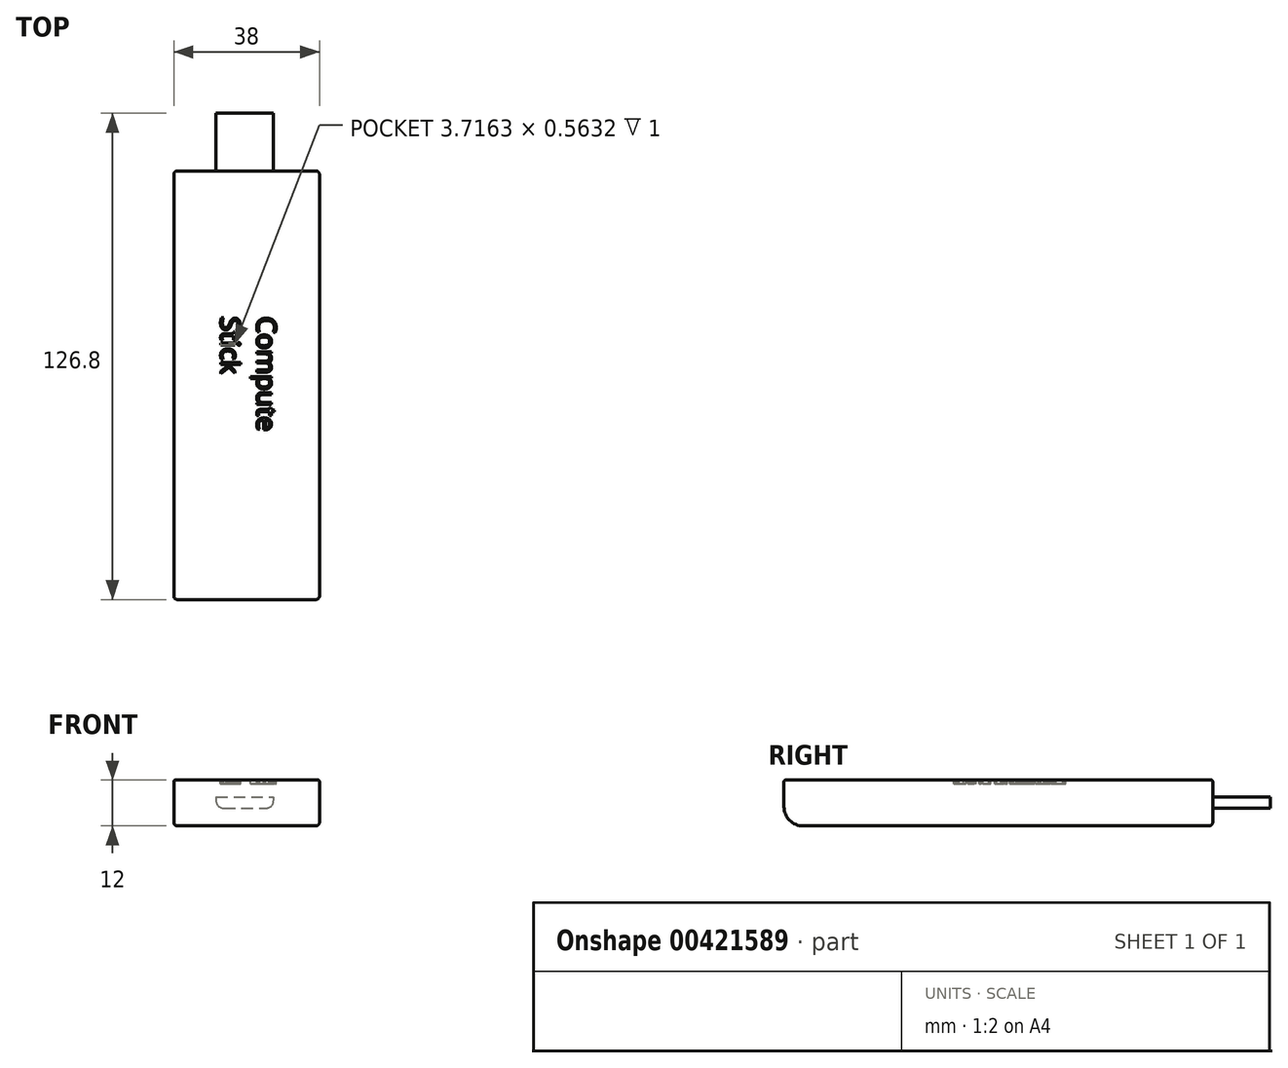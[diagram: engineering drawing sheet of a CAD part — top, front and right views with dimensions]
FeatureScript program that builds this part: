
annotation { "Feature Type Name" : "Feature", "Feature Type Description" : "" }
export const myFeature = defineFeature(function(context is Context, id is Id, definition is map)
    precondition{}
    {
        {
            var Q0;
            Q0=qCreatedBy(makeId("Top.planeOp"),FACE);
            var sketch = newSketch(context, id + "F0", { "sketchPlane" : qUnion([Q0])});
            skLineSegment(sketch, "E0.bottom", {"start": v(-18.53, 32.49) * mm, "end": v(19.47, 32.49) * mm});
            skLineSegment(sketch, "E0.top", {"start": v(-18.53, -79.31) * mm, "end": v(19.47, -79.31) * mm});
            skLineSegment(sketch, "E0.left", {"start": v(-18.53, 32.49) * mm, "end": v(-18.53, -79.31) * mm});
            skLineSegment(sketch, "E0.right", {"start": v(19.47, 32.49) * mm, "end": v(19.47, -79.31) * mm});
            skSolve(sketch);
        }
        {
            var Q0;
            Q0 = qSketchRegion(id + "F0", true);
            extrude(context, id + "F1", {"entities" : qUnion([Q0]), "depth" : 12 * mm, "offsetDistance" : 25 * mm});
        }
        {
            var Q0;
            Q0=makeQuery(id+"F1.opExtrude","SWEPT_EDGE",EDGE,{"disambiguationData":[OSD([sQuery(id+"F0.wireOp",EDGE,"E0.top"),sQuery(id+"F0.wireOp",EDGE,"E0.right")])]});
            var Q1;
            Q1=makeQuery(id+"F1.opExtrude","SWEPT_EDGE",EDGE,{"disambiguationData":[OSD([sQuery(id+"F0.wireOp",EDGE,"E0.top"),sQuery(id+"F0.wireOp",EDGE,"E0.left")])]});
            var Q2;
            Q2=makeQuery(id+"F1.opExtrude","SWEPT_EDGE",EDGE,{"disambiguationData":[OSD([sQuery(id+"F0.wireOp",EDGE,"E0.bottom"),sQuery(id+"F0.wireOp",EDGE,"E0.left")])]});
            var Q3;
            Q3=makeQuery(id+"F1.opExtrude","SWEPT_EDGE",EDGE,{"disambiguationData":[OSD([sQuery(id+"F0.wireOp",EDGE,"E0.bottom"),sQuery(id+"F0.wireOp",EDGE,"E0.right")])]});
            fillet(context, id + "F2", {"entities" : qUnion([Q0, Q1, Q2, Q3]), "radius" : 1 * mm, "tangentPropagation" : true, "allowEdgeOverflow" : false});
        }
        {
            var Q0;
            Q0=makeQuery(id+"F1.opExtrude","CAP_EDGE",EDGE,{"disambiguationData":[OSD([sQuery(id+"F0.wireOp",EDGE,"E0.top")])],"isStart":true});
            fillet(context, id + "F3", {"entities" : qUnion([Q0]), "radius" : 5 * mm, "allowEdgeOverflow" : false});
        }
        {
            var Q0;
            Q0=makeQuery(id+"F3.opFillet","BLEND_EDGE",EDGE,{"blendedFrom":[makeQuery(id+"F1.opExtrude","CAP_EDGE",EDGE,{"disambiguationData":[OSD([sQuery(id+"F0.wireOp",EDGE,"E0.top")])],"isStart":true}),makeQuery(id+"F1.opExtrude","SWEPT_FACE",FACE,{"disambiguationData":[OSD([sQuery(id+"F0.wireOp",EDGE,"E0.left")])]})],"blendedInto":[makeQuery(id+"F1.opExtrude","SWEPT_FACE",FACE,{"disambiguationData":[OSD([sQuery(id+"F0.wireOp",EDGE,"E0.left")])]})]});
            var Q1;
            Q1=makeQuery(id+"F1.opExtrude","CAP_EDGE",EDGE,{"disambiguationData":[OSD([sQuery(id+"F0.wireOp",EDGE,"E0.left")])],"isStart":true});
            var Q2;
            Q2=makeQuery(id+"F1.opExtrude","CAP_EDGE",EDGE,{"disambiguationData":[OSD([sQuery(id+"F0.wireOp",EDGE,"E0.right")])],"isStart":true});
            var Q3;
            Q3=makeQuery(id+"F3.opFillet","BLEND_EDGE",EDGE,{"blendedFrom":[makeQuery(id+"F1.opExtrude","CAP_EDGE",EDGE,{"disambiguationData":[OSD([sQuery(id+"F0.wireOp",EDGE,"E0.top")])],"isStart":true}),makeQuery(id+"F1.opExtrude","SWEPT_FACE",FACE,{"disambiguationData":[OSD([sQuery(id+"F0.wireOp",EDGE,"E0.right")])]})],"blendedInto":[makeQuery(id+"F1.opExtrude","SWEPT_FACE",FACE,{"disambiguationData":[OSD([sQuery(id+"F0.wireOp",EDGE,"E0.right")])]})]});
            var Q4;
            Q4=makeQuery(id+"F1.opExtrude","CAP_EDGE",EDGE,{"disambiguationData":[OSD([sQuery(id+"F0.wireOp",EDGE,"E0.bottom")])],"isStart":true});
            var Q5;
            {var subQ0=sQuery(id+"F0.wireOp",EDGE,"E0.right");var subQ1=sQuery(id+"F0.wireOp",EDGE,"E0.bottom");Q5=makeQuery(id+"F2.opFillet","BLEND_EDGE",EDGE,{"blendedFrom":[makeQuery(id+"F1.opExtrude","SWEPT_EDGE",EDGE,{"disambiguationData":[OSD([subQ1,subQ0])]}),makeQuery(id+"F1.opExtrude","CAP_FACE",FACE,{"disambiguationData":[OSD([subQ1,sQuery(id+"F0.wireOp",EDGE,"E0.top"),sQuery(id+"F0.wireOp",EDGE,"E0.left"),subQ0])],"isStart":true})],"blendedInto":[makeQuery(id+"F1.opExtrude","CAP_FACE",FACE,{"disambiguationData":[OSD([subQ1,sQuery(id+"F0.wireOp",EDGE,"E0.top"),sQuery(id+"F0.wireOp",EDGE,"E0.left"),subQ0])],"isStart":true})]});}
            var Q6;
            {var subQ0=sQuery(id+"F0.wireOp",EDGE,"E0.left");var subQ1=sQuery(id+"F0.wireOp",EDGE,"E0.bottom");Q6=makeQuery(id+"F2.opFillet","BLEND_EDGE",EDGE,{"blendedFrom":[makeQuery(id+"F1.opExtrude","SWEPT_EDGE",EDGE,{"disambiguationData":[OSD([subQ1,subQ0])]}),makeQuery(id+"F1.opExtrude","CAP_FACE",FACE,{"disambiguationData":[OSD([subQ1,sQuery(id+"F0.wireOp",EDGE,"E0.top"),subQ0,sQuery(id+"F0.wireOp",EDGE,"E0.right")])],"isStart":true})],"blendedInto":[makeQuery(id+"F1.opExtrude","CAP_FACE",FACE,{"disambiguationData":[OSD([subQ1,sQuery(id+"F0.wireOp",EDGE,"E0.top"),subQ0,sQuery(id+"F0.wireOp",EDGE,"E0.right")])],"isStart":true})]});}
            var Q7;
            {var subQ0=sQuery(id+"F0.wireOp",EDGE,"E0.top");Q7=makeQuery(id+"F3.opFillet","BLEND_EDGE",EDGE,{"blendedFrom":[makeQuery(id+"F1.opExtrude","CAP_EDGE",EDGE,{"disambiguationData":[OSD([subQ0])],"isStart":true}),makeQuery(id+"F2.opFillet","BLEND_FACE",FACE,{"disambiguationData":[OSD([subQ0,sQuery(id+"F0.wireOp",EDGE,"E0.left")])]})],"blendedInto":[makeQuery(id+"F2.opFillet","BLEND_FACE",FACE,{"disambiguationData":[OSD([subQ0,sQuery(id+"F0.wireOp",EDGE,"E0.left")])]})]});}
            var Q8;
            {var subQ0=sQuery(id+"F0.wireOp",EDGE,"E0.top");Q8=makeQuery(id+"F3.opFillet","BLEND_EDGE",EDGE,{"blendedFrom":[makeQuery(id+"F1.opExtrude","CAP_EDGE",EDGE,{"disambiguationData":[OSD([subQ0])],"isStart":true}),makeQuery(id+"F2.opFillet","BLEND_FACE",FACE,{"disambiguationData":[OSD([subQ0,sQuery(id+"F0.wireOp",EDGE,"E0.right")])]})],"blendedInto":[makeQuery(id+"F2.opFillet","BLEND_FACE",FACE,{"disambiguationData":[OSD([subQ0,sQuery(id+"F0.wireOp",EDGE,"E0.right")])]})]});}
            fillet(context, id + "F4", {"entities" : qUnion([Q0, Q1, Q2, Q3, Q4, Q5, Q6, Q7, Q8]), "radius" : 1 * mm, "tangentPropagation" : true, "allowEdgeOverflow" : false});
        }
        {
            var Q0;
            Q0=makeQuery(id+"F1.opExtrude","CAP_EDGE",EDGE,{"disambiguationData":[OSD([sQuery(id+"F0.wireOp",EDGE,"E0.right")])],"isStart":false});
            fillet(context, id + "F5", {"entities" : qUnion([Q0]), "radius" : 0.5 * mm, "tangentPropagation" : true, "allowEdgeOverflow" : false});
        }
        {
            var Q0;
            Q0=makeQuery(id+"F1.opExtrude","SWEPT_FACE",FACE,{"disambiguationData":[OSD([sQuery(id+"F0.wireOp",EDGE,"E0.bottom")])]});
            cPlane(context, id + "F6", {"entities" : qUnion([Q0]), "cplaneType" : CPlaneType.OFFSET, "offset" : 0 * mm, "width" : 150 * mm, "height" : 150 * mm});
        }
        {
            var Q0;
            Q0=qCreatedBy(id+"F6.planeOp",FACE);
            var sketch = newSketch(context, id + "F7", { "sketchPlane" : qUnion([Q0])});
            skLineSegment(sketch, "E1.bottom", {"start": v(7.5, 7.6) * mm, "end": v(-7.5, 7.6) * mm});
            skLineSegment(sketch, "E1.top", {"start": v(7.5, 4.6) * mm, "end": v(-7.5, 4.6) * mm});
            skLineSegment(sketch, "E1.left", {"start": v(7.5, 7.6) * mm, "end": v(7.5, 4.6) * mm});
            skLineSegment(sketch, "E1.right", {"start": v(-7.5, 7.6) * mm, "end": v(-7.5, 4.6) * mm});
            skPoint(sketch, "E1.middle", {"position": v(0, 6.1) * mm});
            skSolve(sketch);
        }
        {
            var Q0;
            Q0 = qSketchRegion(id + "F7", true);
            extrude(context, id + "F8", {"entities" : qUnion([Q0]), "operationType" : NewBodyOperationType.ADD, "depth" : 15 * mm, "offsetDistance" : 25 * mm});
        }
        {
            var Q0;
            Q0=makeQuery(id+"F8.opExtrude","SWEPT_EDGE",EDGE,{"disambiguationData":[OSD([sQuery(id+"F7.wireOp",EDGE,"E1.top"),sQuery(id+"F7.wireOp",EDGE,"E1.right")])]});
            var Q1;
            Q1=makeQuery(id+"F8.opExtrude","SWEPT_EDGE",EDGE,{"disambiguationData":[OSD([sQuery(id+"F7.wireOp",EDGE,"E1.top"),sQuery(id+"F7.wireOp",EDGE,"E1.left")])]});
            fillet(context, id + "F9", {"entities" : qUnion([Q0, Q1]), "radius" : 2 * mm, "tangentPropagation" : true, "allowEdgeOverflow" : false});
        }
        {
            var Q0;
            Q0=makeQuery(id+"F1.opExtrude","CAP_FACE",FACE,{"disambiguationData":[OSD([sQuery(id+"F0.wireOp",EDGE,"E0.bottom"),sQuery(id+"F0.wireOp",EDGE,"E0.top"),sQuery(id+"F0.wireOp",EDGE,"E0.left"),sQuery(id+"F0.wireOp",EDGE,"E0.right")])],"isStart":false});
            cPlane(context, id + "F10", {"entities" : qUnion([Q0]), "cplaneType" : CPlaneType.OFFSET, "offset" : 0 * mm, "width" : 150 * mm, "height" : 150 * mm});
        }
        {
            var Q0;
            Q0=qCreatedBy(id+"F10.planeOp",FACE);
            var sketch = newSketch(context, id + "F11", { "sketchPlane" : qUnion([Q0])});
            skText(sketch, "E2", { "text": "Compute\nStick", "fontName": "OpenSans-Regular.ttf"});
            const initialGuessF11  = {"E2": [0.00316, -0.0055, 0, -1, 0.005]};
            skSetInitialGuess(sketch, initialGuessF11);
            skSolve(sketch);
        }
        {
            var Q0;
            Q0 = qSketchRegion(id + "F11", true);
            extrude(context, id + "F12", {"entities" : qUnion([Q0]), "operationType" : NewBodyOperationType.REMOVE, "oppositeDirection" : true, "depth" : 1 * mm, "offsetDistance" : 25 * mm});
        }
    });
